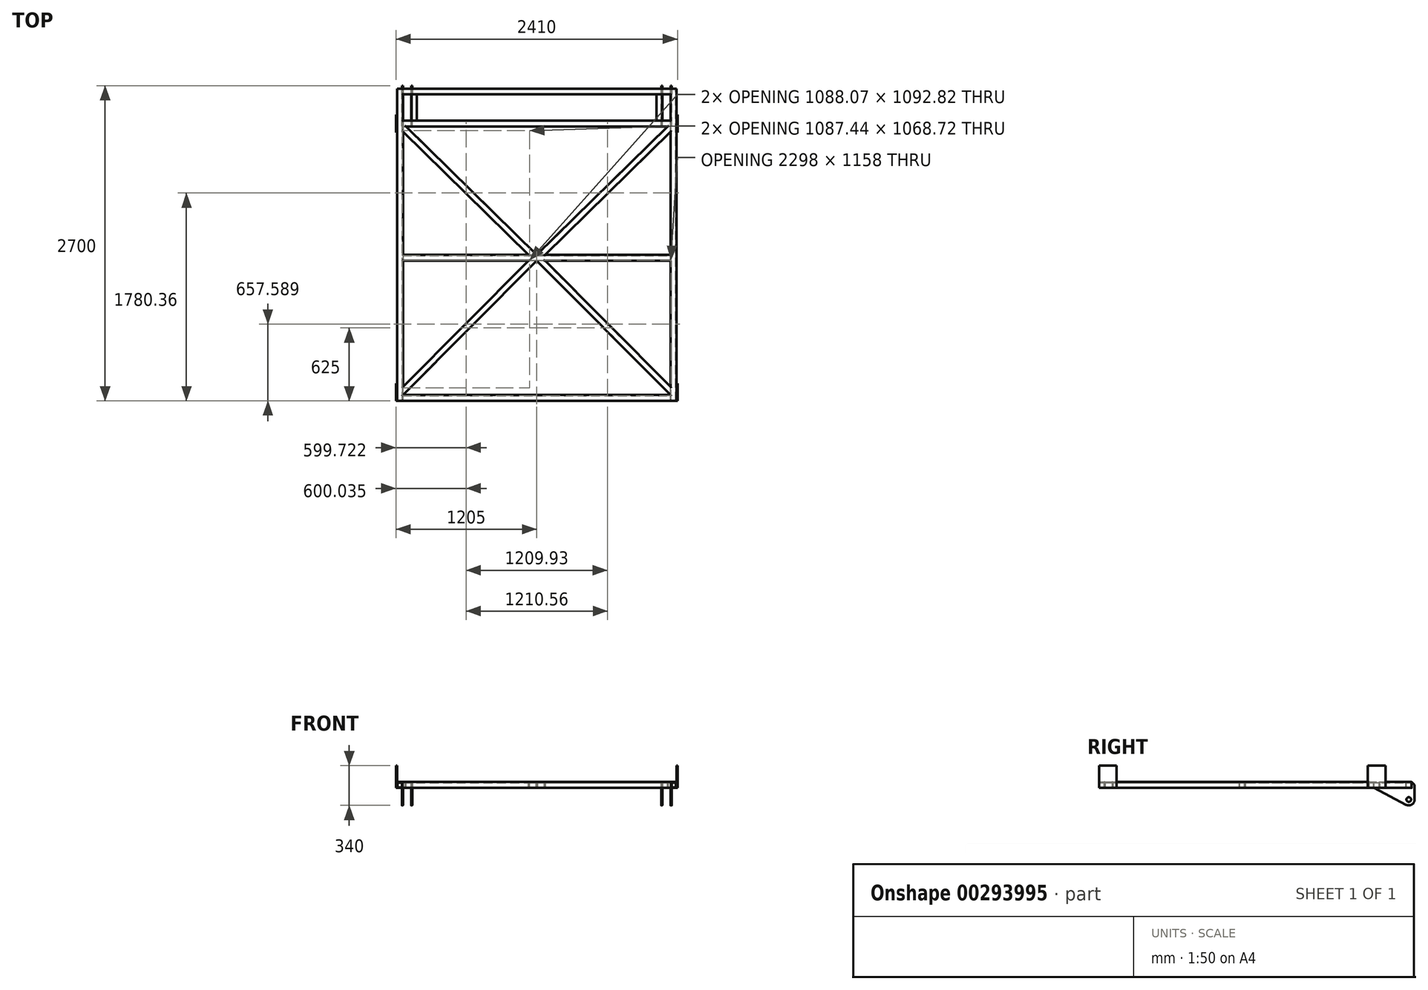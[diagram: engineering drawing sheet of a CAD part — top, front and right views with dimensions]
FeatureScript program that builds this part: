
annotation { "Feature Type Name" : "Feature", "Feature Type Description" : "" }
export const myFeature = defineFeature(function(context is Context, id is Id, definition is map)
    precondition{}
    {
        {
            assignVariable(context, id + "F0", {"name" : "wall_h", "anyValue" : 50});
        }
        {
            var Q0;
            Q0=qCreatedBy(makeId("Top.planeOp"),FACE);
            var sketch = newSketch(context, id + "F1", { "sketchPlane" : qUnion([Q0])});
            skLineSegment(sketch, "E0", {"start": v(1145, 2636.87) * mm, "end": v(1145, -2636.3) * mm, "construction": true});
            skLineSegment(sketch, "E1.MirrorCS", {"start": v(-1145, 2636.87) * mm, "end": v(-1145, -2636.3) * mm, "construction": true});
            skLineSegment(sketch, "E2", {"start": v(0, 0) * mm, "end": v(-1145, 0) * mm, "construction": true});
            skLineSegment(sketch, "E3", {"start": v(0, -2300) * mm, "end": v(-1145, -2300) * mm, "construction": true});
            skLineSegment(sketch, "E4", {"start": v(0, 307.04) * mm, "end": v(0, -2644.6) * mm, "construction": true});
            skLineSegment(sketch, "E5", {"start": v(0, 300) * mm, "end": v(-1145, 300) * mm, "construction": true});
            skLineSegment(sketch, "E6", {"start": v(0, -2375) * mm, "end": v(-1145, -2375) * mm, "construction": true});
            skPoint(sketch, "E7", {"position": v(0, -1150) * mm});
            skSolve(sketch);
        }
        {
            var Q0;
            Q0=qCreatedBy(makeId("Front.planeOp"),FACE);
            cPlane(context, id + "F2", {"entities" : qUnion([Q0]), "cplaneType" : CPlaneType.OFFSET, "offset" : 300 * mm, "oppositeDirection" : true, "width" : 150 * mm, "height" : 150 * mm});
        }
        {
            var Q0;
            Q0=qCreatedBy(id+"F2.planeOp",FACE);
            var sketch = newSketch(context, id + "F3", { "sketchPlane" : qUnion([Q0])});
            skLineSegment(sketch, "E8.bottom", {"start": v(-1191, 0) * mm, "end": v(-1149, 0) * mm});
            skLineSegment(sketch, "E8.top", {"start": v(-1191, -50) * mm, "end": v(-1149, -50) * mm});
            skLineSegment(sketch, "E8.left", {"start": v(-1195, -4) * mm, "end": v(-1195, -46) * mm});
            skLineSegment(sketch, "E8.right", {"start": v(-1145, -4) * mm, "end": v(-1145, -46) * mm});
            skPoint(sketch, "E8.middle", {"position": v(-1170, -25) * mm});
            skLineSegment(sketch, "E9.0", {"start": v(-1189, -4) * mm, "end": v(-1151, -4) * mm});
            skLineSegment(sketch, "E9.1", {"start": v(-1191, -6) * mm, "end": v(-1191, -44) * mm});
            skLineSegment(sketch, "E9.2", {"start": v(-1189, -46) * mm, "end": v(-1151, -46) * mm});
            skLineSegment(sketch, "E9.3", {"start": v(-1149, -6) * mm, "end": v(-1149, -44) * mm});
            skPoint(sketch, "E10.visualSharp", {"position": v(-1195, 0) * mm});
            skArc(sketch, "E10.filletArc", {"start": v(-1191, 0) * mm, "mid": v(-1193.83, -1.17) * mm, "end": v(-1195, -4) * mm});
            skPoint(sketch, "E11.visualSharp", {"position": v(-1145, 0) * mm});
            skArc(sketch, "E11.filletArc", {"start": v(-1145, -4) * mm, "mid": v(-1146.17, -1.17) * mm, "end": v(-1149, 0) * mm});
            skPoint(sketch, "E12.visualSharp", {"position": v(-1145, -50) * mm});
            skArc(sketch, "E12.filletArc", {"start": v(-1149, -50) * mm, "mid": v(-1146.17, -48.83) * mm, "end": v(-1145, -46) * mm});
            skPoint(sketch, "E13.visualSharp", {"position": v(-1195, -50) * mm});
            skArc(sketch, "E13.filletArc", {"start": v(-1195, -46) * mm, "mid": v(-1193.83, -48.83) * mm, "end": v(-1191, -50) * mm});
            skArc(sketch, "E14.filletArc", {"start": v(-1189, -4) * mm, "mid": v(-1190.41, -4.59) * mm, "end": v(-1191, -6) * mm});
            skArc(sketch, "E15.filletArc", {"start": v(-1149, -6) * mm, "mid": v(-1149.59, -4.59) * mm, "end": v(-1151, -4) * mm});
            skArc(sketch, "E16.filletArc", {"start": v(-1151, -46) * mm, "mid": v(-1149.59, -45.41) * mm, "end": v(-1149, -44) * mm});
            skArc(sketch, "E17.filletArc", {"start": v(-1191, -44) * mm, "mid": v(-1190.41, -45.41) * mm, "end": v(-1189, -46) * mm});
            skSolve(sketch);
        }
        {
            var Q0;
            Q0=makeQuery(id+"F3.imprint","IMPRINT",FACE,{"disambiguationData":[TD([[makeQuery(id+"F3.imprint","IMPRINT",EDGE,{"derivedFrom":sQuery(id+"F3.wireOp",EDGE,"E8.bottom")}),-1.0]])]});
            var Q1;
            Q1=sQuery(id+"F1.wireOp",VERTEX,"E6.end");
            extrude(context, id + "F4", {"entities" : qUnion([Q0]), "endBound" : BoundingType.UP_TO_VERTEX, "endBoundEntityVertex" : qUnion([Q1]), "depth" : 25 * mm});
        }
        {
            var Q0;
            Q0=qCreatedBy(makeId("Top.planeOp"),FACE);
            cPlane(context, id + "F5", {"entities" : qUnion([Q0]), "cplaneType" : CPlaneType.OFFSET, "offset" : 100 * mm, "width" : 150 * mm, "height" : 150 * mm});
        }
        {
            var Q0;
            Q0=makeQuery(id+"F4.opExtrude","SWEPT_FACE",FACE,{"disambiguationData":[OSD([sQuery(id+"F3.wireOp",EDGE,"E8.top")])]});
            var sketch = newSketch(context, id + "F6", { "sketchPlane" : qUnion([Q0])});
            skLineSegment(sketch, "E18.0", {"start": v(-1195, 2375) * mm, "end": v(-1195, -300) * mm});
            skLineSegment(sketch, "E19.0", {"start": v(0, 2300) * mm, "end": v(-1145, 2300) * mm});
            skLineSegment(sketch, "E20.0", {"start": v(0, 0) * mm, "end": v(-1145, 0) * mm});
            skLineSegment(sketch, "E21.bottom", {"start": v(-1195, -75) * mm, "end": v(-1205, -75) * mm});
            skLineSegment(sketch, "E21.top", {"start": v(-1195, 75) * mm, "end": v(-1205, 75) * mm});
            skLineSegment(sketch, "E21.left", {"start": v(-1195, -75) * mm, "end": v(-1195, 75) * mm});
            skLineSegment(sketch, "E21.right", {"start": v(-1205, -75) * mm, "end": v(-1205, 75) * mm});
            skLineSegment(sketch, "E22.bottom", {"start": v(-1195, 2375) * mm, "end": v(-1205, 2375) * mm});
            skLineSegment(sketch, "E22.top", {"start": v(-1195, 2225) * mm, "end": v(-1205, 2225) * mm});
            skLineSegment(sketch, "E22.left", {"start": v(-1195, 2375) * mm, "end": v(-1195, 2225) * mm});
            skLineSegment(sketch, "E22.right", {"start": v(-1205, 2375) * mm, "end": v(-1205, 2225) * mm});
            skSolve(sketch);
        }
        {
            var Q0;
            Q0 = qSketchRegion(id + "F6", true);
            extrude(context, id + "F7", {"entities" : qUnion([Q0]), "operationType" : NewBodyOperationType.ADD, "oppositeDirection" : true, "depth" : (getVariable(context, 'wall_h') + 140) * mm});
        }
        {
            var Q0;
            Q0=qCreatedBy(makeId("Right.planeOp"),FACE);
            var sketch = newSketch(context, id + "F8", { "sketchPlane" : qUnion([Q0])});
            skLineSegment(sketch, "E23.bottom", {"start": v(254, 0) * mm, "end": v(296, 0) * mm});
            skLineSegment(sketch, "E23.top", {"start": v(254, -50) * mm, "end": v(296, -50) * mm});
            skLineSegment(sketch, "E23.left", {"start": v(250, -4) * mm, "end": v(250, -46) * mm});
            skLineSegment(sketch, "E23.right", {"start": v(300, -4) * mm, "end": v(300, -46) * mm});
            skPoint(sketch, "E23.middle", {"position": v(275, -25) * mm});
            skLineSegment(sketch, "E24.0", {"start": v(256, -4) * mm, "end": v(294, -4) * mm});
            skLineSegment(sketch, "E24.1", {"start": v(254, -6) * mm, "end": v(254, -44) * mm});
            skLineSegment(sketch, "E24.2", {"start": v(256, -46) * mm, "end": v(294, -46) * mm});
            skLineSegment(sketch, "E24.3", {"start": v(296, -6) * mm, "end": v(296, -44) * mm});
            skPoint(sketch, "E25.visualSharp", {"position": v(250, 0) * mm});
            skArc(sketch, "E25.filletArc", {"start": v(254, 0) * mm, "mid": v(251.17, -1.17) * mm, "end": v(250, -4) * mm});
            skPoint(sketch, "E26.visualSharp", {"position": v(300, 0) * mm});
            skArc(sketch, "E26.filletArc", {"start": v(300, -4) * mm, "mid": v(298.83, -1.17) * mm, "end": v(296, 0) * mm});
            skPoint(sketch, "E27.visualSharp", {"position": v(300, -50) * mm});
            skArc(sketch, "E27.filletArc", {"start": v(296, -50) * mm, "mid": v(298.83, -48.83) * mm, "end": v(300, -46) * mm});
            skPoint(sketch, "E28.visualSharp", {"position": v(250, -50) * mm});
            skArc(sketch, "E28.filletArc", {"start": v(250, -46) * mm, "mid": v(251.17, -48.83) * mm, "end": v(254, -50) * mm});
            skArc(sketch, "E29.filletArc", {"start": v(256, -4) * mm, "mid": v(254.59, -4.59) * mm, "end": v(254, -6) * mm});
            skArc(sketch, "E30.filletArc", {"start": v(296, -6) * mm, "mid": v(295.41, -4.59) * mm, "end": v(294, -4) * mm});
            skArc(sketch, "E31.filletArc", {"start": v(294, -46) * mm, "mid": v(295.41, -45.41) * mm, "end": v(296, -44) * mm});
            skArc(sketch, "E32.filletArc", {"start": v(254, -44) * mm, "mid": v(254.59, -45.41) * mm, "end": v(256, -46) * mm});
            skLineSegment(sketch, "E33.bottom", {"start": v(-2371, 0) * mm, "end": v(-2329, 0) * mm});
            skLineSegment(sketch, "E33.top", {"start": v(-2371, -50) * mm, "end": v(-2329, -50) * mm});
            skLineSegment(sketch, "E33.left", {"start": v(-2375, -4) * mm, "end": v(-2375, -46) * mm});
            skLineSegment(sketch, "E33.right", {"start": v(-2325, -4) * mm, "end": v(-2325, -46) * mm});
            skPoint(sketch, "E33.middle", {"position": v(-2350, -25) * mm});
            skLineSegment(sketch, "E34.0", {"start": v(-2369, -4) * mm, "end": v(-2331, -4) * mm});
            skLineSegment(sketch, "E34.1", {"start": v(-2371, -6) * mm, "end": v(-2371, -44) * mm});
            skLineSegment(sketch, "E34.2", {"start": v(-2369, -46) * mm, "end": v(-2331, -46) * mm});
            skLineSegment(sketch, "E34.3", {"start": v(-2329, -6) * mm, "end": v(-2329, -44) * mm});
            skPoint(sketch, "E35.visualSharp", {"position": v(-2375, 0) * mm});
            skArc(sketch, "E35.filletArc", {"start": v(-2371, 0) * mm, "mid": v(-2373.83, -1.17) * mm, "end": v(-2375, -4) * mm});
            skPoint(sketch, "E36.visualSharp", {"position": v(-2325, 0) * mm});
            skArc(sketch, "E36.filletArc", {"start": v(-2325, -4) * mm, "mid": v(-2326.17, -1.17) * mm, "end": v(-2329, 0) * mm});
            skPoint(sketch, "E37.visualSharp", {"position": v(-2325, -50) * mm});
            skArc(sketch, "E37.filletArc", {"start": v(-2329, -50) * mm, "mid": v(-2326.17, -48.83) * mm, "end": v(-2325, -46) * mm});
            skPoint(sketch, "E38.visualSharp", {"position": v(-2375, -50) * mm});
            skArc(sketch, "E38.filletArc", {"start": v(-2375, -46) * mm, "mid": v(-2373.83, -48.83) * mm, "end": v(-2371, -50) * mm});
            skArc(sketch, "E39.filletArc", {"start": v(-2369, -4) * mm, "mid": v(-2370.41, -4.59) * mm, "end": v(-2371, -6) * mm});
            skArc(sketch, "E40.filletArc", {"start": v(-2329, -6) * mm, "mid": v(-2329.59, -4.59) * mm, "end": v(-2331, -4) * mm});
            skArc(sketch, "E41.filletArc", {"start": v(-2331, -46) * mm, "mid": v(-2329.59, -45.41) * mm, "end": v(-2329, -44) * mm});
            skArc(sketch, "E42.filletArc", {"start": v(-2371, -44) * mm, "mid": v(-2370.41, -45.41) * mm, "end": v(-2369, -46) * mm});
            skLineSegment(sketch, "E43.bottom", {"start": v(-1171, 0) * mm, "end": v(-1129, 0) * mm});
            skLineSegment(sketch, "E43.top", {"start": v(-1171, -50) * mm, "end": v(-1129, -50) * mm});
            skLineSegment(sketch, "E43.left", {"start": v(-1175, -4) * mm, "end": v(-1175, -46) * mm});
            skLineSegment(sketch, "E43.right", {"start": v(-1125, -4) * mm, "end": v(-1125, -46) * mm});
            skPoint(sketch, "E43.middle", {"position": v(-1150, -25) * mm});
            skLineSegment(sketch, "E44.0", {"start": v(-1169, -4) * mm, "end": v(-1131, -4) * mm});
            skLineSegment(sketch, "E44.1", {"start": v(-1171, -6) * mm, "end": v(-1171, -44) * mm});
            skLineSegment(sketch, "E44.2", {"start": v(-1169, -46) * mm, "end": v(-1131, -46) * mm});
            skLineSegment(sketch, "E44.3", {"start": v(-1129, -6) * mm, "end": v(-1129, -44) * mm});
            skPoint(sketch, "E45.visualSharp", {"position": v(-1175, 0) * mm});
            skArc(sketch, "E45.filletArc", {"start": v(-1171, 0) * mm, "mid": v(-1173.83, -1.17) * mm, "end": v(-1175, -4) * mm});
            skPoint(sketch, "E46.visualSharp", {"position": v(-1125, 0) * mm});
            skArc(sketch, "E46.filletArc", {"start": v(-1125, -4) * mm, "mid": v(-1126.17, -1.17) * mm, "end": v(-1129, 0) * mm});
            skPoint(sketch, "E47.visualSharp", {"position": v(-1125, -50) * mm});
            skArc(sketch, "E47.filletArc", {"start": v(-1129, -50) * mm, "mid": v(-1126.17, -48.83) * mm, "end": v(-1125, -46) * mm});
            skPoint(sketch, "E48.visualSharp", {"position": v(-1175, -50) * mm});
            skArc(sketch, "E48.filletArc", {"start": v(-1175, -46) * mm, "mid": v(-1173.83, -48.83) * mm, "end": v(-1171, -50) * mm});
            skArc(sketch, "E49.filletArc", {"start": v(-1169, -4) * mm, "mid": v(-1170.41, -4.59) * mm, "end": v(-1171, -6) * mm});
            skArc(sketch, "E50.filletArc", {"start": v(-1129, -6) * mm, "mid": v(-1129.59, -4.59) * mm, "end": v(-1131, -4) * mm});
            skArc(sketch, "E51.filletArc", {"start": v(-1131, -46) * mm, "mid": v(-1129.59, -45.41) * mm, "end": v(-1129, -44) * mm});
            skArc(sketch, "E52.filletArc", {"start": v(-1171, -44) * mm, "mid": v(-1170.41, -45.41) * mm, "end": v(-1169, -46) * mm});
            skLineSegment(sketch, "E53.bottom", {"start": v(-21, 0) * mm, "end": v(21, 0) * mm});
            skLineSegment(sketch, "E53.top", {"start": v(-21, -50) * mm, "end": v(21, -50) * mm});
            skLineSegment(sketch, "E53.left", {"start": v(-25, -4) * mm, "end": v(-25, -46) * mm});
            skLineSegment(sketch, "E53.right", {"start": v(25, -4) * mm, "end": v(25, -46) * mm});
            skPoint(sketch, "E53.middle", {"position": v(0, -25) * mm});
            skLineSegment(sketch, "E54.0", {"start": v(-19, -4) * mm, "end": v(19, -4) * mm});
            skLineSegment(sketch, "E54.1", {"start": v(-21, -6) * mm, "end": v(-21, -44) * mm});
            skLineSegment(sketch, "E54.2", {"start": v(-19, -46) * mm, "end": v(19, -46) * mm});
            skLineSegment(sketch, "E54.3", {"start": v(21, -6) * mm, "end": v(21, -44) * mm});
            skPoint(sketch, "E55.visualSharp", {"position": v(-25, 0) * mm});
            skArc(sketch, "E55.filletArc", {"start": v(-21, 0) * mm, "mid": v(-23.83, -1.17) * mm, "end": v(-25, -4) * mm});
            skPoint(sketch, "E56.visualSharp", {"position": v(25, 0) * mm});
            skArc(sketch, "E56.filletArc", {"start": v(25, -4) * mm, "mid": v(23.83, -1.17) * mm, "end": v(21, 0) * mm});
            skPoint(sketch, "E57.visualSharp", {"position": v(25, -50) * mm});
            skArc(sketch, "E57.filletArc", {"start": v(21, -50) * mm, "mid": v(23.83, -48.83) * mm, "end": v(25, -46) * mm});
            skPoint(sketch, "E58.visualSharp", {"position": v(-25, -50) * mm});
            skArc(sketch, "E58.filletArc", {"start": v(-25, -46) * mm, "mid": v(-23.83, -48.83) * mm, "end": v(-21, -50) * mm});
            skArc(sketch, "E59.filletArc", {"start": v(-19, -4) * mm, "mid": v(-20.41, -4.59) * mm, "end": v(-21, -6) * mm});
            skArc(sketch, "E60.filletArc", {"start": v(21, -6) * mm, "mid": v(20.41, -4.59) * mm, "end": v(19, -4) * mm});
            skArc(sketch, "E61.filletArc", {"start": v(19, -46) * mm, "mid": v(20.41, -45.41) * mm, "end": v(21, -44) * mm});
            skArc(sketch, "E62.filletArc", {"start": v(-21, -44) * mm, "mid": v(-20.41, -45.41) * mm, "end": v(-19, -46) * mm});
            skSolve(sketch);
        }
        {
            var Q0;
            Q0 = qSketchRegion(id + "F8", true);
            extrude(context, id + "F9", {"entities" : qUnion([Q0]), "operationType" : NewBodyOperationType.ADD, "endBound" : BoundingType.UP_TO_NEXT, "oppositeDirection" : true, "depth" : 25 * mm});
        }
        {
            var Q0;
            Q0=qCreatedBy(makeId("Top.planeOp"),FACE);
            var sketch = newSketch(context, id + "F10", { "sketchPlane" : qUnion([Q0])});
            skPoint(sketch, "E63.0", {"position": v(-1145, 0.29) * mm});
            skLineSegment(sketch, "E64.0", {"start": v(-1145, -1125) * mm, "end": v(0, -1125) * mm, "construction": true});
            skLineSegment(sketch, "E65.0", {"start": v(-1145, -1175) * mm, "end": v(0, -1175) * mm, "construction": true});
            skLineSegment(sketch, "E66.0", {"start": v(-1145, -2325) * mm, "end": v(0, -2325) * mm});
            skLineSegment(sketch, "E67.0", {"start": v(-1145, 2636.87) * mm, "end": v(-1145, -2636.3) * mm, "construction": true});
            skLineSegment(sketch, "E68", {"start": v(-1145, 0.29) * mm, "end": v(0, -1125) * mm});
            skLineSegment(sketch, "E69", {"start": v(0, -1175) * mm, "end": v(-1145, -2325) * mm});
            skPoint(sketch, "E70", {"position": v(-572.5, -1750) * mm});
            skPoint(sketch, "E71", {"position": v(-572.5, -562.36) * mm});
            skLineSegment(sketch, "E72", {"start": v(-572.5, -1750) * mm, "end": v(-803.44, -1520.07) * mm, "construction": true});
            skLineSegment(sketch, "E73", {"start": v(-572.5, -562.36) * mm, "end": v(-768.13, -761.4) * mm, "construction": true});
            skSolve(sketch);
        }
        {
            var Q0;
            Q0=sQuery(id+"F10.wireOp",EDGE,"E73");
            cPoint(context, id + "F11", {"entities" : qUnion([Q0]), "parameter" : 0.5});
        }
        {
            var Q0;
            Q0=sQuery(id+"F10.wireOp",EDGE,"E68");
            var Q1;
            Q1 = qCreatedBy(id + "F11" ,VERTEX);
            cPlane(context, id + "F12", {"entities" : qUnion([Q0, Q1]), "cplaneType" : CPlaneType.LINE_POINT, "offset" : 25 * mm, "width" : 150 * mm, "height" : 150 * mm});
        }
        {
            var Q0;
            Q0=sQuery(id+"F10.wireOp",EDGE,"E72");
            cPoint(context, id + "F13", {"entities" : qUnion([Q0]), "parameter" : 0.5});
        }
        {
            var Q0;
            Q0=sQuery(id+"F10.wireOp",EDGE,"E69");
            var Q1;
            Q1 = qCreatedBy(id + "F13" ,VERTEX);
            cPlane(context, id + "F14", {"entities" : qUnion([Q0, Q1]), "cplaneType" : CPlaneType.LINE_POINT, "offset" : 25 * mm, "width" : 150 * mm, "height" : 150 * mm});
        }
        {
            var Q0;
            Q0=qCreatedBy(id+"F12.planeOp",FACE);
            var sketch = newSketch(context, id + "F15", { "sketchPlane" : qUnion([Q0])});
            skLineSegment(sketch, "E74.bottom", {"start": v(-848.37, 0) * mm, "end": v(-806.37, 0) * mm});
            skLineSegment(sketch, "E74.top", {"start": v(-848.37, -50) * mm, "end": v(-806.37, -50) * mm});
            skLineSegment(sketch, "E74.left", {"start": v(-852.37, -4) * mm, "end": v(-852.37, -46) * mm});
            skLineSegment(sketch, "E74.right", {"start": v(-802.37, -4) * mm, "end": v(-802.37, -46) * mm});
            skPoint(sketch, "E74.middle", {"position": v(-827.37, -25) * mm});
            skLineSegment(sketch, "E75.0", {"start": v(-846.37, -4) * mm, "end": v(-808.37, -4) * mm});
            skLineSegment(sketch, "E75.1", {"start": v(-848.37, -6) * mm, "end": v(-848.37, -44) * mm});
            skLineSegment(sketch, "E75.2", {"start": v(-846.37, -46) * mm, "end": v(-808.37, -46) * mm});
            skLineSegment(sketch, "E75.3", {"start": v(-806.37, -6) * mm, "end": v(-806.37, -44) * mm});
            skPoint(sketch, "E76.visualSharp", {"position": v(-852.37, 0) * mm});
            skArc(sketch, "E76.filletArc", {"start": v(-848.37, 0) * mm, "mid": v(-851.2, -1.17) * mm, "end": v(-852.37, -4) * mm});
            skPoint(sketch, "E77.visualSharp", {"position": v(-802.37, 0) * mm});
            skArc(sketch, "E77.filletArc", {"start": v(-802.37, -4) * mm, "mid": v(-803.54, -1.17) * mm, "end": v(-806.37, 0) * mm});
            skPoint(sketch, "E78.visualSharp", {"position": v(-802.37, -50) * mm});
            skArc(sketch, "E78.filletArc", {"start": v(-806.37, -50) * mm, "mid": v(-803.54, -48.83) * mm, "end": v(-802.37, -46) * mm});
            skPoint(sketch, "E79.visualSharp", {"position": v(-852.37, -50) * mm});
            skArc(sketch, "E79.filletArc", {"start": v(-852.37, -46) * mm, "mid": v(-851.2, -48.83) * mm, "end": v(-848.37, -50) * mm});
            skArc(sketch, "E80.filletArc", {"start": v(-846.37, -4) * mm, "mid": v(-847.79, -4.59) * mm, "end": v(-848.37, -6) * mm});
            skArc(sketch, "E81.filletArc", {"start": v(-806.37, -6) * mm, "mid": v(-806.96, -4.59) * mm, "end": v(-808.37, -4) * mm});
            skArc(sketch, "E82.filletArc", {"start": v(-808.37, -46) * mm, "mid": v(-806.96, -45.41) * mm, "end": v(-806.37, -44) * mm});
            skArc(sketch, "E83.filletArc", {"start": v(-848.37, -44) * mm, "mid": v(-847.79, -45.41) * mm, "end": v(-846.37, -46) * mm});
            skSolve(sketch);
        }
        {
            var Q0;
            Q0=makeQuery(id+"F15.imprint","IMPRINT",FACE,{"disambiguationData":[TD([[makeQuery(id+"F15.imprint","IMPRINT",EDGE,{"derivedFrom":sQuery(id+"F15.wireOp",EDGE,"E74.bottom")}),-1.0]])]});
            extrude(context, id + "F16", {"entities" : qUnion([Q0]), "operationType" : NewBodyOperationType.ADD, "endBound" : BoundingType.UP_TO_NEXT, "depth" : 25 * mm});
        }
        {
            var Q0;
            Q0 = qSketchRegion(id + "F15", true);
            var Q1;
            Q1=makeQuery(id+"F16.opExtrude","CAP_FACE",FACE,{"disambiguationData":[OSD([sQuery(id+"F15.wireOp",EDGE,"E74.bottom"),sQuery(id+"F15.wireOp",EDGE,"E74.top"),sQuery(id+"F15.wireOp",EDGE,"E74.left"),sQuery(id+"F15.wireOp",EDGE,"E74.right"),sQuery(id+"F15.wireOp",EDGE,"E75.0"),sQuery(id+"F15.wireOp",EDGE,"E75.1"),sQuery(id+"F15.wireOp",EDGE,"E75.2"),sQuery(id+"F15.wireOp",EDGE,"E75.3"),sQuery(id+"F15.wireOp",EDGE,"E76.filletArc"),sQuery(id+"F15.wireOp",EDGE,"E77.filletArc"),sQuery(id+"F15.wireOp",EDGE,"E78.filletArc"),sQuery(id+"F15.wireOp",EDGE,"E79.filletArc"),sQuery(id+"F15.wireOp",EDGE,"E80.filletArc"),sQuery(id+"F15.wireOp",EDGE,"E81.filletArc"),sQuery(id+"F15.wireOp",EDGE,"E82.filletArc"),sQuery(id+"F15.wireOp",EDGE,"E83.filletArc")])],"isStart":true});
            extrude(context, id + "F17", {"entities" : qUnion([Q0, Q1]), "operationType" : NewBodyOperationType.ADD, "endBound" : BoundingType.UP_TO_NEXT, "oppositeDirection" : true, "depth" : 25 * mm});
        }
        {
            var Q0;
            Q0=qCreatedBy(id+"F14.planeOp",FACE);
            var sketch = newSketch(context, id + "F18", { "sketchPlane" : qUnion([Q0])});
            skPoint(sketch, "E84.0", {"position": v(829.04, 0) * mm});
            skLineSegment(sketch, "E85.bottom", {"start": v(783.04, 0) * mm, "end": v(825.04, 0) * mm});
            skLineSegment(sketch, "E85.top", {"start": v(783.04, -50) * mm, "end": v(825.04, -50) * mm});
            skLineSegment(sketch, "E85.left", {"start": v(779.04, -4) * mm, "end": v(779.04, -46) * mm});
            skLineSegment(sketch, "E85.right", {"start": v(829.04, -4) * mm, "end": v(829.04, -46) * mm});
            skPoint(sketch, "E85.middle", {"position": v(804.04, -25) * mm});
            skLineSegment(sketch, "E86.0", {"start": v(785.04, -4) * mm, "end": v(823.04, -4) * mm});
            skLineSegment(sketch, "E86.1", {"start": v(783.04, -6) * mm, "end": v(783.04, -44) * mm});
            skLineSegment(sketch, "E86.2", {"start": v(785.04, -46) * mm, "end": v(823.04, -46) * mm});
            skLineSegment(sketch, "E86.3", {"start": v(825.04, -6) * mm, "end": v(825.04, -44) * mm});
            skPoint(sketch, "E87.visualSharp", {"position": v(779.04, 0) * mm});
            skArc(sketch, "E87.filletArc", {"start": v(783.04, 0) * mm, "mid": v(780.2, -1.17) * mm, "end": v(779.04, -4) * mm});
            skArc(sketch, "E88.filletArc", {"start": v(829.04, -4) * mm, "mid": v(827.87, -1.17) * mm, "end": v(825.04, 0) * mm});
            skPoint(sketch, "E89.visualSharp", {"position": v(829.04, -50) * mm});
            skArc(sketch, "E89.filletArc", {"start": v(825.04, -50) * mm, "mid": v(827.87, -48.83) * mm, "end": v(829.04, -46) * mm});
            skPoint(sketch, "E90.visualSharp", {"position": v(779.04, -50) * mm});
            skArc(sketch, "E90.filletArc", {"start": v(779.04, -46) * mm, "mid": v(780.2, -48.83) * mm, "end": v(783.04, -50) * mm});
            skArc(sketch, "E91.filletArc", {"start": v(785.04, -4) * mm, "mid": v(783.62, -4.59) * mm, "end": v(783.04, -6) * mm});
            skArc(sketch, "E92.filletArc", {"start": v(825.04, -6) * mm, "mid": v(824.45, -4.59) * mm, "end": v(823.04, -4) * mm});
            skArc(sketch, "E93.filletArc", {"start": v(823.04, -46) * mm, "mid": v(824.45, -45.41) * mm, "end": v(825.04, -44) * mm});
            skArc(sketch, "E94.filletArc", {"start": v(783.04, -44) * mm, "mid": v(783.62, -45.41) * mm, "end": v(785.04, -46) * mm});
            skSolve(sketch);
        }
        {
            var Q0;
            Q0=makeQuery(id+"F18.imprint","IMPRINT",FACE,{"disambiguationData":[TD([[makeQuery(id+"F18.imprint","IMPRINT",EDGE,{"derivedFrom":sQuery(id+"F18.wireOp",EDGE,"E85.bottom")}),-1.0]])]});
            extrude(context, id + "F19", {"entities" : qUnion([Q0]), "operationType" : NewBodyOperationType.ADD, "endBound" : BoundingType.UP_TO_NEXT, "depth" : 25 * mm});
        }
        {
            var Q0;
            Q0=makeQuery(id+"F19.opExtrude","CAP_FACE",FACE,{"disambiguationData":[OSD([sQuery(id+"F18.wireOp",EDGE,"E85.bottom"),sQuery(id+"F18.wireOp",EDGE,"E85.top"),sQuery(id+"F18.wireOp",EDGE,"E85.left"),sQuery(id+"F18.wireOp",EDGE,"E85.right"),sQuery(id+"F18.wireOp",EDGE,"E86.0"),sQuery(id+"F18.wireOp",EDGE,"E86.1"),sQuery(id+"F18.wireOp",EDGE,"E86.2"),sQuery(id+"F18.wireOp",EDGE,"E86.3"),sQuery(id+"F18.wireOp",EDGE,"E87.filletArc"),sQuery(id+"F18.wireOp",EDGE,"E88.filletArc"),sQuery(id+"F18.wireOp",EDGE,"E89.filletArc"),sQuery(id+"F18.wireOp",EDGE,"E90.filletArc"),sQuery(id+"F18.wireOp",EDGE,"E91.filletArc"),sQuery(id+"F18.wireOp",EDGE,"E92.filletArc"),sQuery(id+"F18.wireOp",EDGE,"E93.filletArc"),sQuery(id+"F18.wireOp",EDGE,"E94.filletArc")])],"isStart":true});
            extrude(context, id + "F20", {"entities" : qUnion([Q0]), "operationType" : NewBodyOperationType.ADD, "endBound" : BoundingType.UP_TO_NEXT, "depth" : 25 * mm});
        }
        {
            var Q0;
            Q0=qCreatedBy(makeId("Top.planeOp"),FACE);
            cPlane(context, id + "F21", {"entities" : qUnion([Q0]), "cplaneType" : CPlaneType.OFFSET, "offset" : 150 * mm, "oppositeDirection" : true, "width" : 150 * mm, "height" : 150 * mm});
        }
        {
            var Q0;
            Q0=qCreatedBy(id+"F21.planeOp",FACE);
            var sketch = newSketch(context, id + "F22", { "sketchPlane" : qUnion([Q0])});
            skLineSegment(sketch, "E95.0", {"start": v(-1145, 2636.87) * mm, "end": v(-1145, -2636.3) * mm, "construction": true});
            skLineSegment(sketch, "E96.0", {"start": v(0, 300) * mm, "end": v(-1145, 300) * mm, "construction": true});
            skLineSegment(sketch, "E97", {"start": v(-1232.3, 275) * mm, "end": v(-850.3, 275) * mm, "construction": true});
            skSolve(sketch);
        }
        {
            var Q0;
            Q0=qCreatedBy(makeId("Right.planeOp"),FACE);
            cPlane(context, id + "F23", {"entities" : qUnion([Q0]), "cplaneType" : CPlaneType.OFFSET, "offset" : 1145 * mm, "oppositeDirection" : true, "width" : 150 * mm, "height" : 150 * mm});
        }
        {
            var Q0;
            Q0=qCreatedBy(id+"F23.planeOp",FACE);
            var sketch = newSketch(context, id + "F24", { "sketchPlane" : qUnion([Q0])});
            skPoint(sketch, "E98.0", {"position": v(275, -150) * mm});
            skCircle(sketch, "E99", {"center": v(275, -150) * mm, "radius": 20 * mm});
            skSolve(sketch);
        }
        {
            var Q0;
            Q0=qCreatedBy(id+"F23.planeOp",FACE);
            var sketch = newSketch(context, id + "F25", { "sketchPlane" : qUnion([Q0])});
            skCircle(sketch, "E100.0", {"center": v(275, -150) * mm, "radius": 20 * mm, "construction": true});
            skLineSegment(sketch, "E101.0", {"start": v(-2375, -50) * mm, "end": v(300, -50) * mm, "construction": true});
            skLineSegment(sketch, "E102.0", {"start": v(300, -4) * mm, "end": v(300, -46) * mm, "construction": true});
            skPoint(sketch, "E103.0", {"position": v(-75, -50) * mm});
            skPoint(sketch, "E104.0", {"position": v(300, -50) * mm});
            skPoint(sketch, "E105.0", {"position": v(300, 0) * mm});
            skLineSegment(sketch, "E106", {"start": v(325, -29) * mm, "end": v(325, -150) * mm});
            skLineSegment(sketch, "E107", {"start": v(-75, -50) * mm, "end": v(300, -50) * mm});
            skLineSegment(sketch, "E108", {"start": v(300, -50) * mm, "end": v(300, -4) * mm});
            skLineSegment(sketch, "E109", {"start": v(300, 0) * mm, "end": v(325, -25) * mm});
            skLineSegment(sketch, "E110", {"start": v(325, -29) * mm, "end": v(325, -25) * mm});
            skLineSegment(sketch, "E111", {"start": v(300, -4) * mm, "end": v(300, 0) * mm});
            skCircle(sketch, "E112", {"center": v(275, -150) * mm, "radius": 20 * mm});
            skPoint(sketch, "E113.0", {"position": v(-21, -50) * mm});
            skArc(sketch, "E114", {"start": v(251.62, -194.2) * mm, "mid": v(300.8, -192.83) * mm, "end": v(325, -150) * mm});
            skLineSegment(sketch, "E115", {"start": v(-21, -50) * mm, "end": v(251.62, -194.2) * mm});
            skLineSegment(sketch, "E116", {"start": v(-21, -50) * mm, "end": v(300, -50) * mm});
            skSolve(sketch);
        }
        {
            var Q0;
            Q0 = qSketchRegion(id + "F25", true);
            extrude(context, id + "F26", {"entities" : qUnion([Q0]), "oppositeDirection" : true, "depth" : 10 * mm});
        }
        {
            var Q0;
            Q0=qCreatedBy(id+"F23.planeOp",FACE);
            cPlane(context, id + "F27", {"entities" : qUnion([Q0]), "cplaneType" : CPlaneType.OFFSET, "offset" : 80 * mm, "width" : 150 * mm, "height" : 150 * mm});
        }
        {
            var Q0;
            Q0=qCreatedBy(id+"F27.planeOp",FACE);
            var sketch = newSketch(context, id + "F28", { "sketchPlane" : qUnion([Q0])});
            skLineSegment(sketch, "E117.0", {"start": v(300, 0) * mm, "end": v(325, -25) * mm});
            skLineSegment(sketch, "E118.0", {"start": v(325, -25) * mm, "end": v(325, -150) * mm});
            skArc(sketch, "E119.0", {"start": v(251.62, -194.2) * mm, "mid": v(300.8, -192.83) * mm, "end": v(325, -150) * mm});
            skCircle(sketch, "E120.0", {"center": v(275, -150) * mm, "radius": 20 * mm});
            skLineSegment(sketch, "E121.0", {"start": v(-21, -50) * mm, "end": v(251.62, -194.2) * mm});
            skLineSegment(sketch, "E122.0.0", {"start": v(300, -50) * mm, "end": v(300, 0) * mm});
            skArc(sketch, "E122.0.3", {"start": v(325, -150) * mm, "mid": v(300.8, -192.83) * mm, "end": v(251.62, -194.2) * mm});
            skLineSegment(sketch, "E122.0.4", {"start": v(251.62, -194.2) * mm, "end": v(-21, -50) * mm});
            skLineSegment(sketch, "E122.0.5", {"start": v(-21, -50) * mm, "end": v(300, -50) * mm});
            skSolve(sketch);
        }
        {
            var Q0;
            Q0 = qSketchRegion(id + "F28", true);
            extrude(context, id + "F29", {"entities" : qUnion([Q0]), "operationType" : NewBodyOperationType.ADD, "oppositeDirection" : true, "depth" : 10 * mm});
        }
        {
            var Q0;
            Q0=makeQuery(id+"F4.opExtrude","SWEPT_BODY",BODY,{"disambiguationData":[OSD([sQuery(id+"F3.wireOp",EDGE,"E8.bottom"),sQuery(id+"F3.wireOp",EDGE,"E8.top"),sQuery(id+"F3.wireOp",EDGE,"E8.left"),sQuery(id+"F3.wireOp",EDGE,"E8.right"),sQuery(id+"F3.wireOp",EDGE,"E9.0"),sQuery(id+"F3.wireOp",EDGE,"E9.1"),sQuery(id+"F3.wireOp",EDGE,"E9.2"),sQuery(id+"F3.wireOp",EDGE,"E9.3"),sQuery(id+"F3.wireOp",EDGE,"E10.filletArc"),sQuery(id+"F3.wireOp",EDGE,"E11.filletArc"),sQuery(id+"F3.wireOp",EDGE,"E12.filletArc"),sQuery(id+"F3.wireOp",EDGE,"E13.filletArc"),sQuery(id+"F3.wireOp",EDGE,"E14.filletArc"),sQuery(id+"F3.wireOp",EDGE,"E15.filletArc"),sQuery(id+"F3.wireOp",EDGE,"E16.filletArc"),sQuery(id+"F3.wireOp",EDGE,"E17.filletArc")])]});
            var Q1;
            Q1=makeQuery(id+"F26.opExtrude","SWEPT_BODY",BODY,{"disambiguationData":[OSD([sQuery(id+"F25.wireOp",EDGE,"E106"),sQuery(id+"F25.wireOp",EDGE,"E108"),sQuery(id+"F25.wireOp",EDGE,"E109"),sQuery(id+"F25.wireOp",EDGE,"E110"),sQuery(id+"F25.wireOp",EDGE,"E111"),sQuery(id+"F25.wireOp",EDGE,"E112"),sQuery(id+"F25.wireOp",EDGE,"E114"),sQuery(id+"F25.wireOp",EDGE,"E115"),sQuery(id+"F25.wireOp",EDGE,"E116")])]});
            var Q2;
            Q2=qCreatedBy(makeId("Right.planeOp"),FACE);
            mirror(context, id + "F30", {"operationType" : NewBodyOperationType.ADD, "entities" : qUnion([Q0, Q1]), "mirrorPlane" : qUnion([Q2])});
        }
        {
            var Q0;
            Q0=qCreatedBy(makeId("Front.planeOp"),FACE);
            cPlane(context, id + "F31", {"entities" : qUnion([Q0]), "cplaneType" : CPlaneType.OFFSET, "offset" : 137.5 * mm, "oppositeDirection" : true, "width" : 150 * mm, "height" : 150 * mm});
        }
        {
            var Q0;
            Q0=qCreatedBy(id+"F31.planeOp",FACE);
            var sketch = newSketch(context, id + "F32", { "sketchPlane" : qUnion([Q0])});
            skPoint(sketch, "E123.0", {"position": v(-1075, -50) * mm});
            skPoint(sketch, "E124.0", {"position": v(1075, -50) * mm});
            skLineSegment(sketch, "E125", {"start": v(1075, 0) * mm, "end": v(1075, -45) * mm});
            skLineSegment(sketch, "E126", {"start": v(1070, -50) * mm, "end": v(1025, -50) * mm});
            skLineSegment(sketch, "E127", {"start": v(1025, -50) * mm, "end": v(1025, -46) * mm});
            skLineSegment(sketch, "E128", {"start": v(1025, -46) * mm, "end": v(1066, -46) * mm});
            skLineSegment(sketch, "E129", {"start": v(1071, -41) * mm, "end": v(1071, 0) * mm});
            skLineSegment(sketch, "E130", {"start": v(1071, 0) * mm, "end": v(1075, 0) * mm});
            skPoint(sketch, "E131.visualSharp", {"position": v(1071, -46) * mm});
            skArc(sketch, "E131.filletArc", {"start": v(1066, -46) * mm, "mid": v(1069.54, -44.54) * mm, "end": v(1071, -41) * mm});
            skArc(sketch, "E132.filletArc", {"start": v(1070, -50) * mm, "mid": v(1073.54, -48.54) * mm, "end": v(1075, -45) * mm});
            skLineSegment(sketch, "E133", {"start": v(-1025, -50) * mm, "end": v(-1070, -50) * mm});
            skLineSegment(sketch, "E134", {"start": v(-1075, -45) * mm, "end": v(-1075, 0) * mm});
            skLineSegment(sketch, "E135", {"start": v(-1075, 0) * mm, "end": v(-1071, 0) * mm});
            skLineSegment(sketch, "E136", {"start": v(-1071, 0) * mm, "end": v(-1071, -41) * mm});
            skLineSegment(sketch, "E137", {"start": v(-1066, -46) * mm, "end": v(-1025, -46) * mm});
            skLineSegment(sketch, "E138", {"start": v(-1025, -46) * mm, "end": v(-1025, -50) * mm});
            skPoint(sketch, "E139.visualSharp", {"position": v(-1071, -46) * mm});
            skArc(sketch, "E139.filletArc", {"start": v(-1071, -41) * mm, "mid": v(-1069.54, -44.54) * mm, "end": v(-1066, -46) * mm});
            skArc(sketch, "E140.filletArc", {"start": v(-1075, -45) * mm, "mid": v(-1073.54, -48.54) * mm, "end": v(-1070, -50) * mm});
            skSolve(sketch);
        }
        {
            var Q0;
            Q0 = qSketchRegion(id + "F32", true);
            extrude(context, id + "F33", {"entities" : qUnion([Q0]), "operationType" : NewBodyOperationType.ADD, "endBound" : BoundingType.UP_TO_NEXT, "depth" : 225 * mm});
        }
        {
            var Q0;
            Q0=makeQuery(id+"F33.opExtrude","CAP_FACE",FACE,{"disambiguationData":[OSD([sQuery(id+"F32.wireOp",EDGE,"E125"),sQuery(id+"F32.wireOp",EDGE,"E126"),sQuery(id+"F32.wireOp",EDGE,"E127"),sQuery(id+"F32.wireOp",EDGE,"E128"),sQuery(id+"F32.wireOp",EDGE,"E129"),sQuery(id+"F32.wireOp",EDGE,"E130"),sQuery(id+"F32.wireOp",EDGE,"E131.filletArc"),sQuery(id+"F32.wireOp",EDGE,"E132.filletArc")])],"isStart":true});
            var Q1;
            Q1=makeQuery(id+"F33.opExtrude","CAP_FACE",FACE,{"disambiguationData":[OSD([sQuery(id+"F32.wireOp",EDGE,"E133"),sQuery(id+"F32.wireOp",EDGE,"E134"),sQuery(id+"F32.wireOp",EDGE,"E135"),sQuery(id+"F32.wireOp",EDGE,"E136"),sQuery(id+"F32.wireOp",EDGE,"E137"),sQuery(id+"F32.wireOp",EDGE,"E138"),sQuery(id+"F32.wireOp",EDGE,"E139.filletArc"),sQuery(id+"F32.wireOp",EDGE,"E140.filletArc")])],"isStart":true});
            extrude(context, id + "F34", {"entities" : qUnion([Q0, Q1]), "operationType" : NewBodyOperationType.ADD, "endBound" : BoundingType.UP_TO_NEXT, "depth" : 25 * mm});
        }
    });
